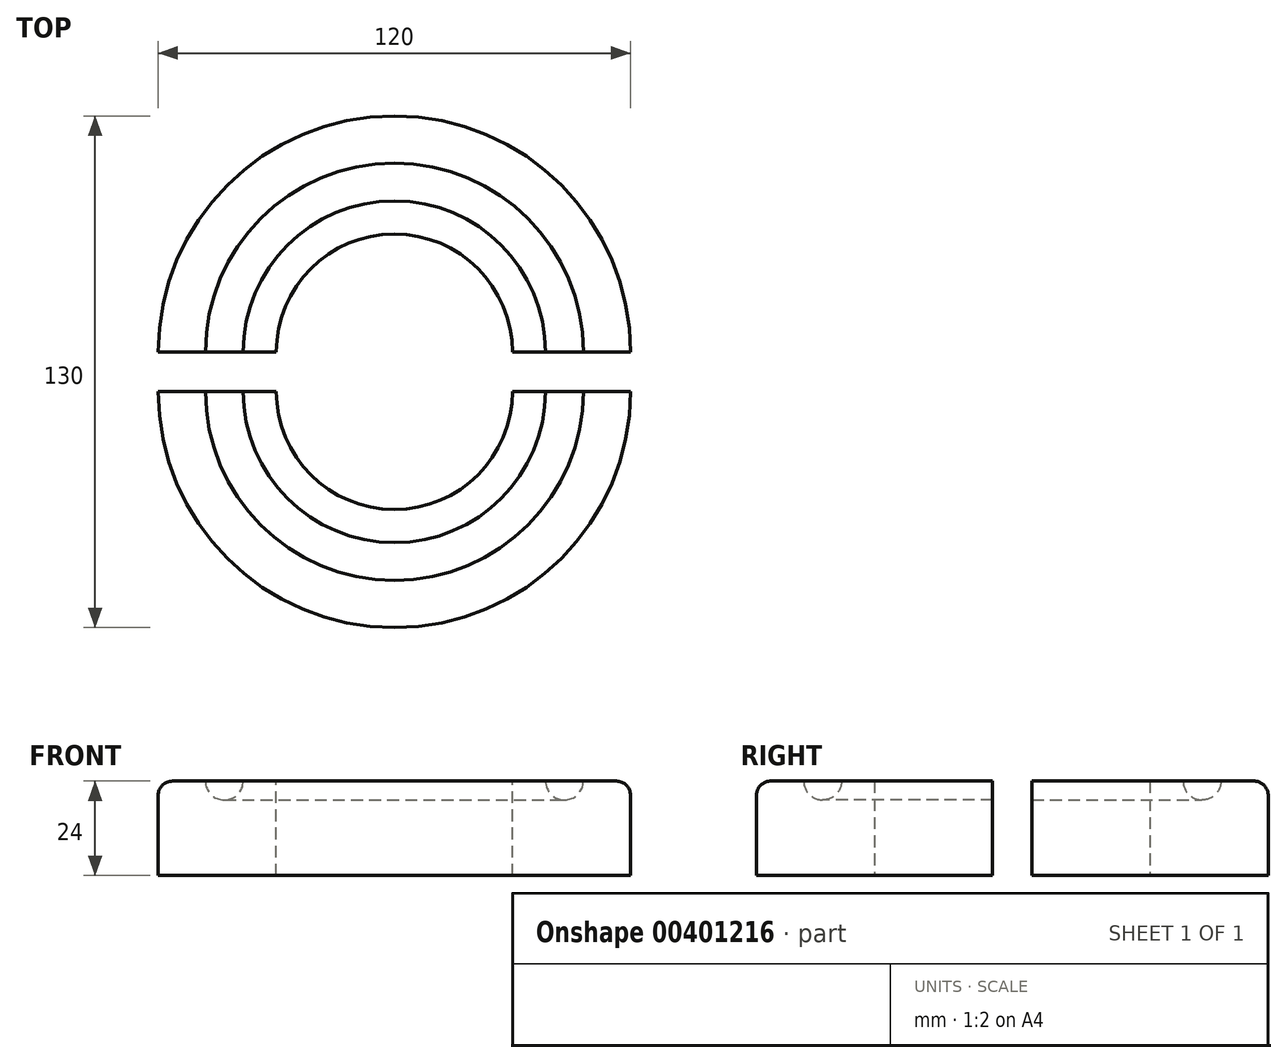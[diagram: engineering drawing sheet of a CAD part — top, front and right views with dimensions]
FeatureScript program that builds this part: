
annotation { "Feature Type Name" : "Feature", "Feature Type Description" : "" }
export const myFeature = defineFeature(function(context is Context, id is Id, definition is map)
    precondition{}
    {
        {
            var Q0;
            Q0=qCreatedBy(makeId("Front.planeOp"),FACE);
            var sketch = newSketch(context, id + "F0", { "sketchPlane" : qUnion([Q0])});
            skLineSegment(sketch, "E0", {"start": v(-60, 0) * mm, "end": v(-60, 20.4) * mm});
            skLineSegment(sketch, "E1", {"start": v(-56.4, 24) * mm, "end": v(-48, 24) * mm});
            skLineSegment(sketch, "E2.MirrorCS", {"start": v(-30, 0) * mm, "end": v(-30, 24) * mm});
            skLineSegment(sketch, "E3.MirrorCS", {"start": v(-30, 24) * mm, "end": v(-38.4, 24) * mm});
            skArc(sketch, "E4", {"start": v(-48, 24) * mm, "mid": v(-43.2, 19.2) * mm, "end": v(-38.4, 24) * mm});
            skLineSegment(sketch, "E5", {"start": v(-60, 0) * mm, "end": v(-30, 0) * mm});
            skLineSegment(sketch, "E6", {"start": v(0, 0) * mm, "end": v(0, 36.08) * mm, "construction": true});
            skArc(sketch, "E7", {"start": v(-60, 20.4) * mm, "mid": v(-58.95, 22.95) * mm, "end": v(-56.4, 24) * mm});
            skSolve(sketch);
        }
        {
            var Q0;
            Q0=makeQuery(id+"F0.imprint","IMPRINT",FACE,{"disambiguationData":[TD([[makeQuery(id+"F0.imprint","IMPRINT",EDGE,{"derivedFrom":sQuery(id+"F0.wireOp",EDGE,"E0")}),-1.0]])]});
            var Q1;
            Q1=sQuery(id+"F0.wireOp",EDGE,"E6");
            revolve(context, id + "F1", {"surfaceOperationType" : NewSurfaceOperationType.NEW, "entities" : qUnion([Q0]), "axis" : qUnion([Q1]), "revolveType" : RevolveType.ONE_DIRECTION, "angle" : 180 * degree});
        }
        {
            var Q0;
            Q0=makeQuery(id+"F1.opRevolve","SWEPT_BODY",BODY,{"disambiguationData":[OSD([sQuery(id+"F0.wireOp",EDGE,"E0"),sQuery(id+"F0.wireOp",EDGE,"E1"),sQuery(id+"F0.wireOp",EDGE,"E2.MirrorCS"),sQuery(id+"F0.wireOp",EDGE,"E3.MirrorCS"),sQuery(id+"F0.wireOp",EDGE,"E4"),sQuery(id+"F0.wireOp",EDGE,"E5")])]});
            var Q1;
            Q1=makeQuery(id+"F1.opRevolve","CAP_FACE",FACE,{"disambiguationData":[OSD([sQuery(id+"F0.wireOp",EDGE,"E0"),sQuery(id+"F0.wireOp",EDGE,"E1"),sQuery(id+"F0.wireOp",EDGE,"E2.MirrorCS"),sQuery(id+"F0.wireOp",EDGE,"E3.MirrorCS"),sQuery(id+"F0.wireOp",EDGE,"E4"),sQuery(id+"F0.wireOp",EDGE,"E5")])],"isStart":false});
            mirror(context, id + "F2", {"entities" : qUnion([Q0]), "mirrorPlane" : qUnion([Q1])});
        }
        {
            var Q0;
            Q0=makeQuery(id+"F1.opRevolve","SWEPT_BODY",BODY,{"disambiguationData":[OSD([sQuery(id+"F0.wireOp",EDGE,"E0"),sQuery(id+"F0.wireOp",EDGE,"E1"),sQuery(id+"F0.wireOp",EDGE,"E2.MirrorCS"),sQuery(id+"F0.wireOp",EDGE,"E3.MirrorCS"),sQuery(id+"F0.wireOp",EDGE,"E4"),sQuery(id+"F0.wireOp",EDGE,"E5"),sQuery(id+"F0.wireOp",EDGE,"E7")])]});
            transform(context, id + "F3", {"entities" : qUnion([Q0]), "transformType" : TransformType.TRANSLATION_3D, "dx" : 0 * mm, "dy" : -10 * mm, "dz" : 0 * mm, "makeCopy" : false});
        }
    });
